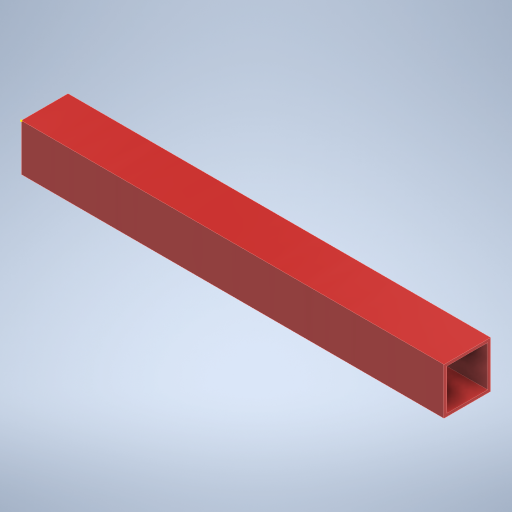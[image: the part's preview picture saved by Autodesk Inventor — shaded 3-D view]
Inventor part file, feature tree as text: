
AUTODESK INVENTOR PART (.ipt)
format: ipt  version: 2024 (Build 280153000, 153)  size: 233,984 bytes
history: native  units: in
note: dims shown in document units (in); Inventor stores cm internally (conversion verified against a paired STEP export)
features: sketch x2, extrude x1
ambient origin geometry x8: Origin, YZ Plane, XZ Plane, XY Plane, X Axis, Y Axis, Z Axis, Center Point
bodies: Solid1 (feature_tree)
feature tree (3):
  extrude  "Extrusion1"  Depth=1.0in
  sketch  "Sketch2"  dims[d2=0.0625in d3=9.0551in d4=0.0in]
  sketch  "Sketch1"  dims[d0=1.0in d1=1.0in]
